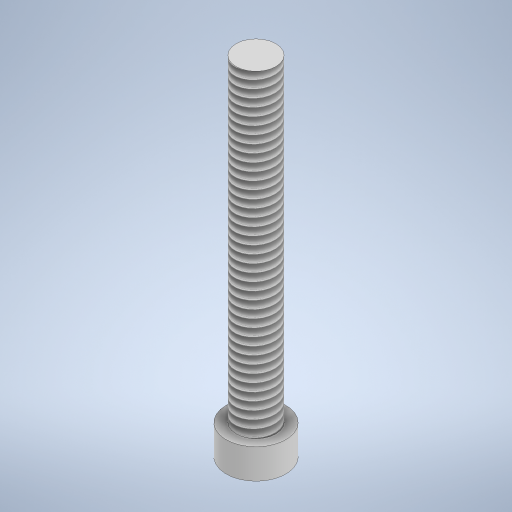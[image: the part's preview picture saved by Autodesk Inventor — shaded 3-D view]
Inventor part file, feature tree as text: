
AUTODESK INVENTOR PART (.ipt)
format: ipt  version: 2024.2 (Build 282272000, 272)  size: 284,672 bytes
history: native  units: mm
features: extrude x2, sketch x2, thread x1
ambient origin geometry x8: Origin, YZ Plane, XZ Plane, XY Plane, X Axis, Y Axis, Z Axis, Center Point
bodies: Solid1 (feature_tree)
feature tree (5):
  extrude  "Extrusion1"  Depth=1.5mm TaperAngle=0.0deg
  extrude  "Extrusion2"  Depth=16.0mm TaperAngle=0.0deg
  thread  "Thread1"  [1 undecoded]
  sketch  "Sketch1"  dims[d0=3.0mm d1=1.5mm d2=0.0mm]
  sketch  "Sketch2"  dims[d3=2.0mm d4=16.0mm d5=0.0mm d6=18.0mm d7=0.0mm]
note: 1 required parameter value undecoded (feature->parameter linkage not recoverable at this tier; creation-order binding heuristic only, values carry confidence <= 0.55)
